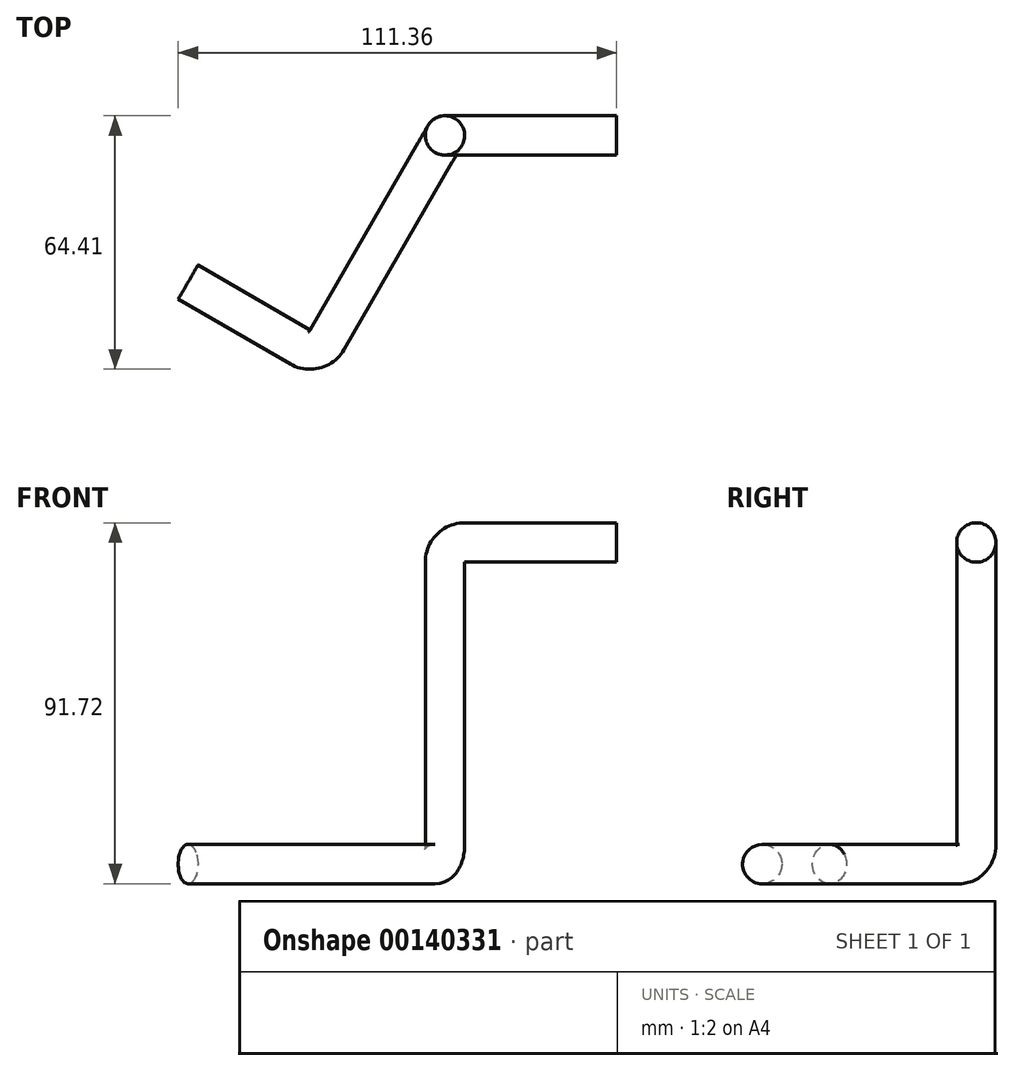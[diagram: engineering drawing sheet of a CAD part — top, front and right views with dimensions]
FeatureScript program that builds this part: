
annotation { "Feature Type Name" : "Feature", "Feature Type Description" : "" }
export const myFeature = defineFeature(function(context is Context, id is Id, definition is map)
    precondition{}
    {
        {
            var Q0;
            Q0=qCreatedBy(makeId("Front.planeOp"),FACE);
            var sketch = newSketch(context, id + "F0", { "sketchPlane" : qUnion([Q0])});
            skLineSegment(sketch, "E0", {"start": v(43.58, 46.96) * mm, "end": v(5, 46.96) * mm});
            skLineSegment(sketch, "E1", {"start": v(0, 41.96) * mm, "end": v(0, -10.96) * mm});
            skPoint(sketch, "E2.visualSharp", {"position": v(0, 46.96) * mm});
            skArc(sketch, "E2.filletArc", {"start": v(5, 46.96) * mm, "mid": v(1.46, 45.5) * mm, "end": v(0, 41.96) * mm});
            skSolve(sketch);
        }
        {
            var Q0;
            Q0=sQuery(id+"F0.wireOp",EDGE,"E1");
            cPlane(context, id + "F1", {"entities" : qUnion([Q0]), "cplaneType" : CPlaneType.LINE_ANGLE, "offset" : 25 * mm, "angle" : 30 * degree, "width" : 150 * mm, "height" : 150 * mm});
        }
        {
            var Q0;
            Q0=qCreatedBy(id+"F1.planeOp",FACE);
            var sketch = newSketch(context, id + "F2", { "sketchPlane" : qUnion([Q0])});
            skPoint(sketch, "E3.0", {"position": v(0, -10.96) * mm});
            skLineSegment(sketch, "E4", {"start": v(0, -10.96) * mm, "end": v(0, -29.76) * mm});
            skLineSegment(sketch, "E5", {"start": v(5, -34.76) * mm, "end": v(29.1, -34.76) * mm});
            skPoint(sketch, "E6.visualSharp", {"position": v(0, -34.76) * mm});
            skArc(sketch, "E6.filletArc", {"start": v(0, -29.76) * mm, "mid": v(1.46, -33.3) * mm, "end": v(5, -34.76) * mm});
            skSolve(sketch);
        }
        {
            var Q0;
            Q0=sQuery(id+"F2.wireOp",VERTEX,"E5.end");
            var Q1;
            Q1=qCreatedBy(makeId("Top.planeOp"),FACE);
            cPlane(context, id + "F3", {"entities" : qUnion([Q0, Q1]), "cplaneType" : CPlaneType.PLANE_POINT, "offset" : 25 * mm, "width" : 150 * mm, "height" : 150 * mm});
        }
        {
            var Q0;
            Q0=qCreatedBy(id+"F3.planeOp",FACE);
            var sketch = newSketch(context, id + "F4", { "sketchPlane" : qUnion([Q0])});
            skPoint(sketch, "E7.0", {"position": v(-14.55, -25.2) * mm});
            skLineSegment(sketch, "E8", {"start": v(-14.55, -25.2) * mm, "end": v(-29.97, -51.9) * mm});
            skLineSegment(sketch, "E9", {"start": v(-36.8, -53.74) * mm, "end": v(-65.28, -37.3) * mm});
            skPoint(sketch, "E10.visualSharp", {"position": v(-32.47, -56.24) * mm});
            skArc(sketch, "E10.filletArc", {"start": v(-36.8, -53.74) * mm, "mid": v(-33, -54.24) * mm, "end": v(-29.97, -51.9) * mm});
            skSolve(sketch);
        }
        {
            var Q0;
            Q0=sQuery(id+"F0.wireOp",VERTEX,"E0.start");
            var Q1;
            Q1=sQuery(id+"F0.wireOp",EDGE,"E0");
            cPlane(context, id + "F5", {"entities" : qUnion([Q0, Q1]), "cplaneType" : CPlaneType.LINE_POINT, "offset" : 25 * mm, "width" : 150 * mm, "height" : 150 * mm});
        }
        {
            var Q0;
            Q0=qCreatedBy(id+"F5.planeOp",FACE);
            var sketch = newSketch(context, id + "F6", { "sketchPlane" : qUnion([Q0])});
            skPoint(sketch, "E11.0", {"position": v(0, 46.96) * mm});
            skCircle(sketch, "E12", {"center": v(0, 46.96) * mm, "radius": 5 * mm});
            skSolve(sketch);
        }
        {
            var Q0;
            Q0=makeQuery(id+"F6.imprint","IMPRINT",FACE,{"disambiguationData":[TD([[makeQuery(id+"F6.imprint","IMPRINT",EDGE,{"derivedFrom":sQuery(id+"F6.wireOp",EDGE,"E12")}),1.0]])]});
            var Q1;
            Q1=sQuery(id+"F0.wireOp",EDGE,"E0");
            var Q2;
            Q2=sQuery(id+"F0.wireOp",EDGE,"E2.filletArc");
            var Q3;
            Q3=sQuery(id+"F0.wireOp",EDGE,"E1");
            var Q4;
            Q4=sQuery(id+"F2.wireOp",EDGE,"E4");
            var Q5;
            Q5=sQuery(id+"F2.wireOp",EDGE,"E6.filletArc");
            var Q6;
            Q6=sQuery(id+"F2.wireOp",EDGE,"E5");
            var Q7;
            Q7=sQuery(id+"F4.wireOp",EDGE,"E8");
            var Q8;
            Q8=sQuery(id+"F4.wireOp",EDGE,"E10.filletArc");
            var Q9;
            Q9=sQuery(id+"F4.wireOp",EDGE,"E9");
            sweep(context, id + "F7", {"profiles" : qUnion([Q0]), "path" : qUnion([Q1, Q2, Q3, Q4, Q5, Q6, Q7, Q8, Q9])});
        }
    });
